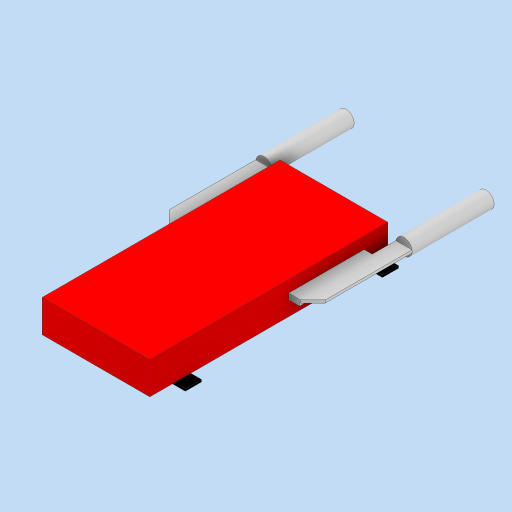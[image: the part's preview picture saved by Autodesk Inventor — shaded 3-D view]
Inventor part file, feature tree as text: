
AUTODESK INVENTOR PART (.ipt)
format: ipt  version: 2023 (Build 270158000, 158)  size: 206,336 bytes
history: native  units: in
note: dims shown in document units (in); Inventor stores cm internally (conversion verified against a paired STEP export)
features: extrude x5, sketch x5, plane x4, mirror x3, projected_geometry x1
ambient origin geometry x8: Origin, YZ Plane, XZ Plane, XY Plane, X Axis, Y Axis, Z Axis, Center Point
bodies: Solid1 (feature_tree)
feature tree (18):
  extrude  "Extrusion1"  Depth=8.7008in
  extrude  "Extrusion2"  Depth=0.9055in
  plane  "Work Plane1"
  extrude  "Extrusion3"  Depth=4.7244in
  plane  "Work Plane2"
  mirror  "Mirror1"
  extrude  "Extrusion4"  Depth=0.8661in
  mirror  "Mirror2"
  plane  "Work Plane4"
  plane  "Work Plane3"
  extrude  "Extrusion5"  Depth=2.7559in
  mirror  "Mirror3"
  sketch  "Sketch1"  dims[d0=3.937in d1=8.7008in]
  sketch  "Sketch2"  dims[d2=1.1811in d3=0.0in d4=0.9055in]
  sketch  "Sketch3"  dims[d5=0.5906in d6=4.7244in]
  sketch  "Sketch4"  dims[d7=0.0787in d8=0.0in d9=0.8661in]
  projected_geometry  "Projected Loop1"
  sketch  "Sketch5"  dims[d10=0.3937in d11=2.7559in d12=0.1181in d13=0.0in d14=0.0591in d15=0.0in d16=-0.5906in d17=0.8858in d19=45.0deg d20=0.4331in d21=0.0984in d22=0.0in d23=0.2953in d24=0.8661in d25=0.0in d26=0.0in d27=3.0in d28=0.0in]
